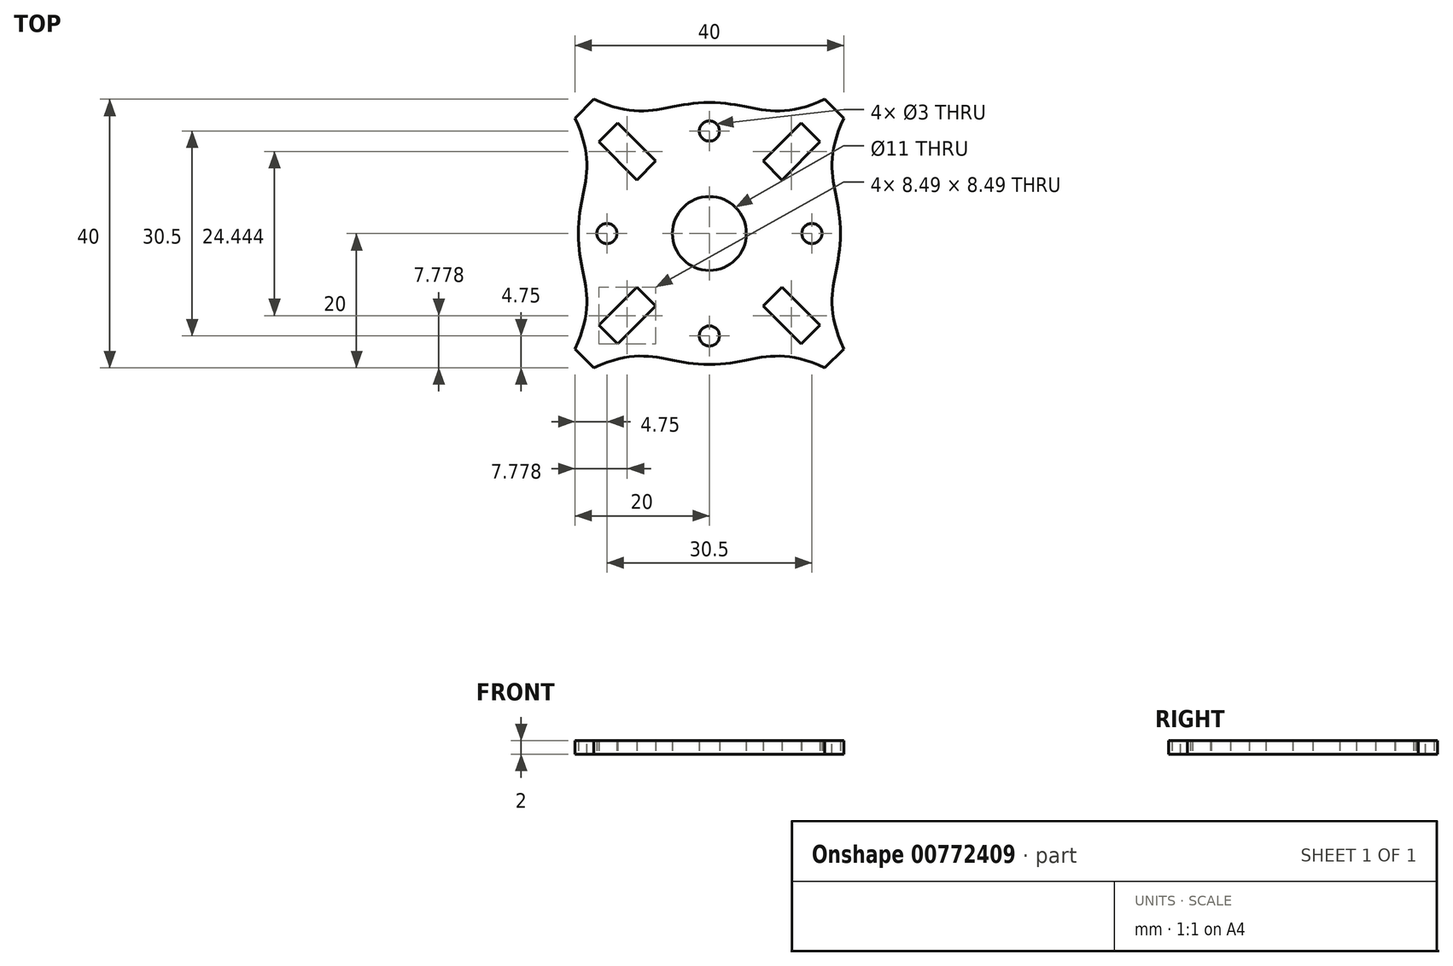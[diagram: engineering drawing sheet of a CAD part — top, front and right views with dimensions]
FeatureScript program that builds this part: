
annotation { "Feature Type Name" : "Feature", "Feature Type Description" : "" }
export const myFeature = defineFeature(function(context is Context, id is Id, definition is map)
    precondition{}
    {
        {
            var Q0;
            Q0=qCreatedBy(makeId("Top.planeOp"),FACE);
            var sketch = newSketch(context, id + "F0", { "sketchPlane" : qUnion([Q0])});
            skLineSegment(sketch, "E0.bottom", {"start": v(20, 20) * mm, "end": v(-20, 20) * mm});
            skLineSegment(sketch, "E0.top", {"start": v(20, -20) * mm, "end": v(-20, -20) * mm});
            skLineSegment(sketch, "E0.left", {"start": v(20, 20) * mm, "end": v(20, -20) * mm});
            skLineSegment(sketch, "E0.right", {"start": v(-20, 20) * mm, "end": v(-20, -20) * mm});
            skPoint(sketch, "E0.middle", {"position": v(0, 0) * mm});
            skLineSegment(sketch, "E1.bottom", {"start": v(-16.46, -13.64) * mm, "end": v(-10.8, -7.98) * mm});
            skLineSegment(sketch, "E1.top", {"start": v(-13.64, -16.46) * mm, "end": v(-7.98, -10.8) * mm});
            skLineSegment(sketch, "E1.left", {"start": v(-16.46, -13.64) * mm, "end": v(-13.64, -16.46) * mm});
            skLineSegment(sketch, "E1.right", {"start": v(-10.8, -7.98) * mm, "end": v(-7.98, -10.8) * mm});
            skLineSegment(sketch, "E2", {"start": v(-20, -17.17) * mm, "end": v(-17.17, -20) * mm});
            skLineSegment(sketch, "E3", {"start": v(-20, -20) * mm, "end": v(-2.4, -2.4) * mm, "construction": true});
            skPoint(sketch, "E4", {"position": v(-15.05, -15.05) * mm});
            skLineSegment(sketch, "E5.1.0", {"start": v(13.64, -16.46) * mm, "end": v(16.46, -13.64) * mm});
            skLineSegment(sketch, "E5.1.1", {"start": v(13.64, -16.46) * mm, "end": v(7.98, -10.8) * mm});
            skLineSegment(sketch, "E5.1.2", {"start": v(7.98, -10.8) * mm, "end": v(10.8, -7.98) * mm});
            skLineSegment(sketch, "E5.1.3", {"start": v(16.46, -13.64) * mm, "end": v(10.8, -7.98) * mm});
            skLineSegment(sketch, "E5.1.4", {"start": v(17.17, -20) * mm, "end": v(20, -17.17) * mm});
            skLineSegment(sketch, "E5.2.0", {"start": v(16.46, 13.64) * mm, "end": v(13.64, 16.46) * mm});
            skLineSegment(sketch, "E5.2.1", {"start": v(16.46, 13.64) * mm, "end": v(10.8, 7.98) * mm});
            skLineSegment(sketch, "E5.2.2", {"start": v(10.8, 7.98) * mm, "end": v(7.98, 10.8) * mm});
            skLineSegment(sketch, "E5.2.3", {"start": v(13.64, 16.46) * mm, "end": v(7.98, 10.8) * mm});
            skLineSegment(sketch, "E5.2.4", {"start": v(20, 17.17) * mm, "end": v(17.17, 20) * mm});
            skLineSegment(sketch, "E5.3.0", {"start": v(-13.64, 16.46) * mm, "end": v(-16.46, 13.64) * mm});
            skLineSegment(sketch, "E5.3.1", {"start": v(-13.64, 16.46) * mm, "end": v(-7.98, 10.8) * mm});
            skLineSegment(sketch, "E5.3.2", {"start": v(-7.98, 10.8) * mm, "end": v(-10.8, 7.98) * mm});
            skLineSegment(sketch, "E5.3.3", {"start": v(-16.46, 13.64) * mm, "end": v(-10.8, 7.98) * mm});
            skLineSegment(sketch, "E5.3.4", {"start": v(-17.17, 20) * mm, "end": v(-20, 17.17) * mm});
            skCircle(sketch, "E6", {"center": v(0, 0) * mm, "radius": 5.5 * mm});
            skCircle(sketch, "E7", {"center": v(0, 15.25) * mm, "radius": 1.5 * mm});
            skCircle(sketch, "E8.1.0", {"center": v(-15.25, 0) * mm, "radius": 1.5 * mm});
            skCircle(sketch, "E8.2.0", {"center": v(0, -15.25) * mm, "radius": 1.5 * mm});
            skCircle(sketch, "E8.3.0", {"center": v(15.25, 0) * mm, "radius": 1.5 * mm});
            skFitSpline(sketch, "E9", {"points": [v(-17.17, -20) * mm, v(0, -19.5) * mm], "startDerivative": vector(23.46, 10.92) * mm, "endDerivative": vector(19.6, 0) * mm});
            skFitSpline(sketch, "E10.MirrorCS", {"points": [v(17.17, -20) * mm, v(0, -19.5) * mm], "startDerivative": vector(-23.46, 10.92) * mm, "endDerivative": vector(-19.6, 0) * mm});
            skSolve(sketch);
        }
        {
            var Q0;
            Q0=makeQuery(id+"F0.imprint","IMPRINT",FACE,{"disambiguationData":[TD([[makeQuery(id+"F0.imprint","IMPRINT",EDGE,{"derivedFrom":sQuery(id+"F0.wireOp",EDGE,"E1.bottom")}),1.0]])]});
            var Q1;
            {var subQ0=sQuery(id+"F0.wireOp",EDGE,"E9");Q1=makeQuery(id+"F0.imprint","IMPRINT",FACE,{"disambiguationData":[TD([[makeQuery(id+"F0.imprint","IMPRINT",EDGE,{"derivedFrom":subQ0}),-1.0]])]});}
            var Q2;
            {var subQ0=sQuery(id+"F0.wireOp",EDGE,"E10.MirrorCS");Q2=makeQuery(id+"F0.imprint","IMPRINT",FACE,{"disambiguationData":[TD([[makeQuery(id+"F0.imprint","IMPRINT",EDGE,{"derivedFrom":subQ0}),1.0]])]});}
            extrude(context, id + "F1", {"entities" : qUnion([Q0, Q1, Q2]), "depth" : 2 * mm, "offsetDistance" : 25 * mm});
        }
        {
            var Q0;
            {var subQ0=sQuery(id+"F0.wireOp",EDGE,"E9");Q0=makeQuery(id+"F0.imprint","IMPRINT",FACE,{"disambiguationData":[TD([[makeQuery(id+"F0.imprint","IMPRINT",EDGE,{"derivedFrom":subQ0}),-1.0]])]});}
            var Q1;
            {var subQ0=sQuery(id+"F0.wireOp",EDGE,"E10.MirrorCS");Q1=makeQuery(id+"F0.imprint","IMPRINT",FACE,{"disambiguationData":[TD([[makeQuery(id+"F0.imprint","IMPRINT",EDGE,{"derivedFrom":subQ0}),1.0]])]});}
            extrude(context, id + "F2", {"entities" : qUnion([Q0, Q1]), "depth" : 2 * mm, "offsetDistance" : 25 * mm});
        }
        {
            var Q0;
            Q0=makeQuery(id+"F2.opExtrude","SWEPT_BODY",BODY,{"disambiguationData":[OSD([sQuery(id+"F0.wireOp",EDGE,"E0.top"),sQuery(id+"F0.wireOp",EDGE,"E9"),sQuery(id+"F0.wireOp",EDGE,"E10.MirrorCS")])]});
            var Q1;
            Q1=makeQuery(id+"F1.opExtrude","CAP_EDGE",EDGE,{"disambiguationData":[OSD([sQuery(id+"F0.wireOp",EDGE,"E6")])],"isStart":false});
            circularPattern(context, id + "F3", {"operationType" : NewBodyOperationType.REMOVE, "entities" : qUnion([Q0]), "axis" : qUnion([Q1]), "angle" : 360 * degree, "instanceCount" : 4, "equalSpace" : true});
        }
    });
